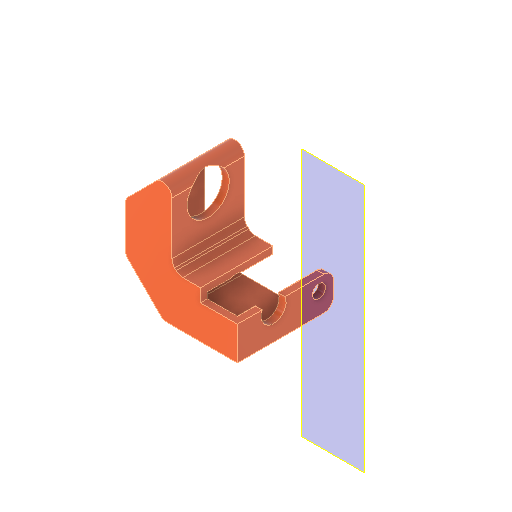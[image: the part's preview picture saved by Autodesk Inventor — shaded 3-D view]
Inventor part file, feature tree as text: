
AUTODESK INVENTOR PART (.ipt)
format: ipt  version: 2022 (Build 260153000, 153)  size: 278,016 bytes
history: native  units: in
note: dims shown in document units (in); Inventor stores cm internally (conversion verified against a paired STEP export)
features: other x8, extrude x7, sketch x6, reference x5, projected_geometry x2, plane x1, fillet x1
ambient origin geometry x8: Origin, YZ Plane, XZ Plane, XY Plane, X Axis, Y Axis, Z Axis, Center Point
bodies: Solid1 (feature_tree)
feature tree (30):
  plane  "Work Plane1"
  extrude  "Extrusion1"  Depth=0.5512in TaperAngle=0.0deg
  extrude  "Extrusion2"  Depth=0.0591in
  extrude  "Extrusion3"  TaperAngle=135.0deg  [1 undecoded]
  extrude  "Extrusion8"  Depth=0.2362in
  extrude  "Extrusion9"  Depth=0.2362in
  extrude  "Extrusion11"  Depth=0.5512in TaperAngle=0.0deg
  extrude  "Extrusion12"  Depth=0.0591in
  fillet  "Rundung1"  Radius=0.0591in
  sketch  "Sketch2"  dims[d0=0.0591in d1=0.0in d3=0.5512in d4=0.0in]
  sketch  "Sketch3"  dims[d12=0.0591in d13=0.0in d22=0.5307in]
  reference  "Reference1"
  projected_geometry  "Projected Loop5"
  projected_geometry  "Projected Loop6"
  sketch  "Sketch8"  dims[d23=0.2653in d25=135.0deg]
  reference  "Reference2"
  reference  "Reference3"
  sketch  "Sketch9"  dims[d26=0.1575in d27=0.2362in]
  reference  "Reference4"
  sketch  "Skizze11"  dims[d28=0.1568in d29=0.2362in]
  sketch  "Skizze12"  dims[d31=0.3937in d35=0.5512in d36=0.0in d40=0.0591in d41=0.0591in d42=0.9449in d43=0.5512in d44=0.0in d45=0.0in d48=0.0in d49=0.0in d50=0.1969in d51=0.3937in d52=0.0in d53=0.0787in]
  reference  "Referenz5"
  other  "<userpath>\Documents\Matchboxscope\INVENTOR\Matchboxscope_v0.iam"
  other  "Matchboxscope_v0.iam"
  other  "Matchboxscope_sample_v0:1"
  other  "Matchboxscope_middle2_v1:1"
  other  "00_ESP3-CAM:5"
  other  "Bauteil50"
  other  "Assembly_Matchboxscope_injectionmolded.iam"
  other  "IM_Matchboxscope_plate:2"
note: 1 required parameter value undecoded (feature->parameter linkage not recoverable at this tier; creation-order binding heuristic only, values carry confidence <= 0.55)
